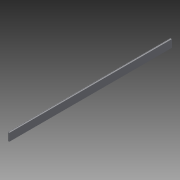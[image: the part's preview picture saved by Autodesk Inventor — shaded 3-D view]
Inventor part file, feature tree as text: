
AUTODESK INVENTOR PART (.ipt)
format: ipt  version: 2015 SP1 (Build 190203100, 203)  size: 79,360 bytes
history: native  units: in
note: dims shown in document units (in); Inventor stores cm internally (conversion verified against a paired STEP export)
features: extrude x1, sketch x1
ambient origin geometry x8: Origin, YZ Plane, XZ Plane, XY Plane, X Axis, Y Axis, Z Axis, Center Point
bodies: Solid1 (feature_tree)
feature tree (2):
  extrude  "Extrusion1"  Depth=0.6299in
  sketch  "Sketch1"  dims[d0=3.937in d1=0.6299in d2=78.7402in d3=0.0in d4=0.1181in d5=0.1181in d6=0.0787in d7=0.2362in]
